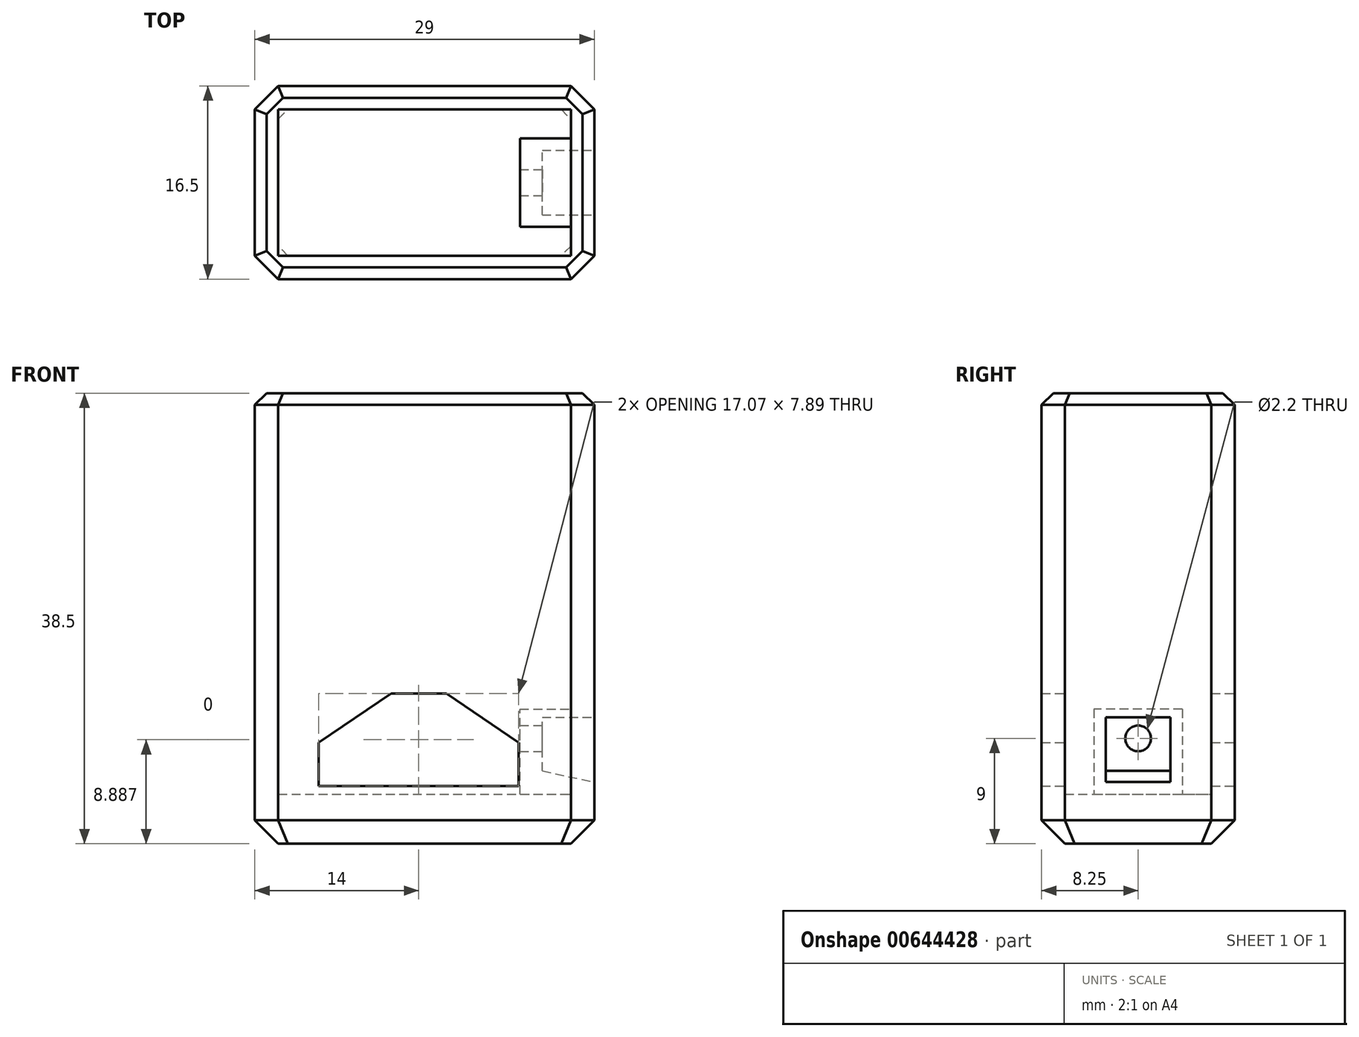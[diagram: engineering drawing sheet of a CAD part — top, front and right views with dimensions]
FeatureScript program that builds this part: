
annotation { "Feature Type Name" : "Feature", "Feature Type Description" : "" }
export const myFeature = defineFeature(function(context is Context, id is Id, definition is map)
    precondition{}
    {
        {
            var Q0;
            Q0=qCreatedBy(makeId("Top.planeOp"),FACE);
            var sketch = newSketch(context, id + "F0", { "sketchPlane" : qUnion([Q0])});
            skLineSegment(sketch, "E0.bottom", {"start": v(0, 0) * mm, "end": v(29, 0) * mm});
            skLineSegment(sketch, "E0.top", {"start": v(0, 16.5) * mm, "end": v(29, 16.5) * mm});
            skLineSegment(sketch, "E0.left", {"start": v(0, 0) * mm, "end": v(0, 16.5) * mm});
            skLineSegment(sketch, "E0.right", {"start": v(29, 0) * mm, "end": v(29, 16.5) * mm});
            skSolve(sketch);
        }
        {
            var Q0;
            Q0 = qSketchRegion(id + "F0", true);
            extrude(context, id + "F1", {"entities" : qUnion([Q0]), "depth" : 38.5 * mm, "offsetDistance" : 25 * mm});
        }
        {
            var Q0;
            Q0=makeQuery(id+"F1.opExtrude","CAP_FACE",FACE,{"disambiguationData":[OSD([sQuery(id+"F0.wireOp",EDGE,"E0.bottom"),sQuery(id+"F0.wireOp",EDGE,"E0.top"),sQuery(id+"F0.wireOp",EDGE,"E0.left"),sQuery(id+"F0.wireOp",EDGE,"E0.right")])],"isStart":false});
            shell(context, id + "F2", {"entities" : qUnion([Q0]), "thickness" : 2 * mm});
        }
        {
            var Q0;
            Q0=makeQuery(id+"F2.opShell","OFFSET_FACE",FACE,{"disambiguationData":[OSD([sQuery(id+"F0.wireOp",EDGE,"E0.bottom"),sQuery(id+"F0.wireOp",EDGE,"E0.top"),sQuery(id+"F0.wireOp",EDGE,"E0.left"),sQuery(id+"F0.wireOp",EDGE,"E0.right")])]});
            extrude(context, id + "F3", {"entities" : qUnion([Q0]), "operationType" : NewBodyOperationType.ADD, "depth" : 2.25 * mm, "offsetDistance" : 25 * mm});
        }
        {
            var Q0;
            Q0=makeQuery(id+"F1.opExtrude","SWEPT_EDGE",EDGE,{"disambiguationData":[OSD([sQuery(id+"F0.wireOp",EDGE,"E0.bottom"),sQuery(id+"F0.wireOp",EDGE,"E0.right")])]});
            var Q1;
            Q1=makeQuery(id+"F1.opExtrude","SWEPT_EDGE",EDGE,{"disambiguationData":[OSD([sQuery(id+"F0.wireOp",EDGE,"E0.top"),sQuery(id+"F0.wireOp",EDGE,"E0.right")])]});
            var Q2;
            Q2=makeQuery(id+"F1.opExtrude","SWEPT_EDGE",EDGE,{"disambiguationData":[OSD([sQuery(id+"F0.wireOp",EDGE,"E0.bottom"),sQuery(id+"F0.wireOp",EDGE,"E0.left")])]});
            var Q3;
            Q3=makeQuery(id+"F1.opExtrude","SWEPT_EDGE",EDGE,{"disambiguationData":[OSD([sQuery(id+"F0.wireOp",EDGE,"E0.top"),sQuery(id+"F0.wireOp",EDGE,"E0.left")])]});
            chamfer(context, id + "F4", {"entities" : qUnion([Q0, Q1, Q2, Q3]), "width" : 2 * mm, "tangentPropagation" : true});
        }
        {
            var Q0;
            Q0=makeQuery(id+"F1.opExtrude","CAP_EDGE",EDGE,{"disambiguationData":[OSD([sQuery(id+"F0.wireOp",EDGE,"E0.bottom")])],"isStart":true});
            var Q1;
            {var subQ0=sQuery(id+"F0.wireOp",EDGE,"E0.right");var subQ1=sQuery(id+"F0.wireOp",EDGE,"E0.bottom");Q1=makeQuery(id+"F4.opChamfer","BLEND_EDGE",EDGE,{"blendedFrom":[makeQuery(id+"F1.opExtrude","SWEPT_EDGE",EDGE,{"disambiguationData":[OSD([subQ1,subQ0])]}),makeQuery(id+"F1.opExtrude","CAP_FACE",FACE,{"disambiguationData":[OSD([subQ1,sQuery(id+"F0.wireOp",EDGE,"E0.top"),sQuery(id+"F0.wireOp",EDGE,"E0.left"),subQ0])],"isStart":true})],"blendedInto":[makeQuery(id+"F1.opExtrude","CAP_FACE",FACE,{"disambiguationData":[OSD([subQ1,sQuery(id+"F0.wireOp",EDGE,"E0.top"),sQuery(id+"F0.wireOp",EDGE,"E0.left"),subQ0])],"isStart":true})]});}
            var Q2;
            Q2=makeQuery(id+"F1.opExtrude","CAP_EDGE",EDGE,{"disambiguationData":[OSD([sQuery(id+"F0.wireOp",EDGE,"E0.right")])],"isStart":true});
            var Q3;
            {var subQ0=sQuery(id+"F0.wireOp",EDGE,"E0.right");var subQ1=sQuery(id+"F0.wireOp",EDGE,"E0.top");Q3=makeQuery(id+"F4.opChamfer","BLEND_EDGE",EDGE,{"blendedFrom":[makeQuery(id+"F1.opExtrude","SWEPT_EDGE",EDGE,{"disambiguationData":[OSD([subQ1,subQ0])]}),makeQuery(id+"F1.opExtrude","CAP_FACE",FACE,{"disambiguationData":[OSD([sQuery(id+"F0.wireOp",EDGE,"E0.bottom"),subQ1,sQuery(id+"F0.wireOp",EDGE,"E0.left"),subQ0])],"isStart":true})],"blendedInto":[makeQuery(id+"F1.opExtrude","CAP_FACE",FACE,{"disambiguationData":[OSD([sQuery(id+"F0.wireOp",EDGE,"E0.bottom"),subQ1,sQuery(id+"F0.wireOp",EDGE,"E0.left"),subQ0])],"isStart":true})]});}
            var Q4;
            Q4=makeQuery(id+"F1.opExtrude","CAP_EDGE",EDGE,{"disambiguationData":[OSD([sQuery(id+"F0.wireOp",EDGE,"E0.top")])],"isStart":true});
            var Q5;
            {var subQ0=sQuery(id+"F0.wireOp",EDGE,"E0.left");var subQ1=sQuery(id+"F0.wireOp",EDGE,"E0.top");Q5=makeQuery(id+"F4.opChamfer","BLEND_EDGE",EDGE,{"blendedFrom":[makeQuery(id+"F1.opExtrude","SWEPT_EDGE",EDGE,{"disambiguationData":[OSD([subQ1,subQ0])]}),makeQuery(id+"F1.opExtrude","CAP_FACE",FACE,{"disambiguationData":[OSD([sQuery(id+"F0.wireOp",EDGE,"E0.bottom"),subQ1,subQ0,sQuery(id+"F0.wireOp",EDGE,"E0.right")])],"isStart":true})],"blendedInto":[makeQuery(id+"F1.opExtrude","CAP_FACE",FACE,{"disambiguationData":[OSD([sQuery(id+"F0.wireOp",EDGE,"E0.bottom"),subQ1,subQ0,sQuery(id+"F0.wireOp",EDGE,"E0.right")])],"isStart":true})]});}
            var Q6;
            Q6=makeQuery(id+"F1.opExtrude","CAP_EDGE",EDGE,{"disambiguationData":[OSD([sQuery(id+"F0.wireOp",EDGE,"E0.left")])],"isStart":true});
            var Q7;
            {var subQ0=sQuery(id+"F0.wireOp",EDGE,"E0.left");var subQ1=sQuery(id+"F0.wireOp",EDGE,"E0.bottom");Q7=makeQuery(id+"F4.opChamfer","BLEND_EDGE",EDGE,{"blendedFrom":[makeQuery(id+"F1.opExtrude","SWEPT_EDGE",EDGE,{"disambiguationData":[OSD([subQ1,subQ0])]}),makeQuery(id+"F1.opExtrude","CAP_FACE",FACE,{"disambiguationData":[OSD([subQ1,sQuery(id+"F0.wireOp",EDGE,"E0.top"),subQ0,sQuery(id+"F0.wireOp",EDGE,"E0.right")])],"isStart":true})],"blendedInto":[makeQuery(id+"F1.opExtrude","CAP_FACE",FACE,{"disambiguationData":[OSD([subQ1,sQuery(id+"F0.wireOp",EDGE,"E0.top"),subQ0,sQuery(id+"F0.wireOp",EDGE,"E0.right")])],"isStart":true})]});}
            chamfer(context, id + "F5", {"entities" : qUnion([Q0, Q1, Q2, Q3, Q4, Q5, Q6, Q7]), "width" : 2 * mm, "tangentPropagation" : true});
        }
        {
            var Q0;
            Q0=makeQuery(id+"F1.opExtrude","CAP_EDGE",EDGE,{"disambiguationData":[OSD([sQuery(id+"F0.wireOp",EDGE,"E0.left")])],"isStart":false});
            var Q1;
            {var subQ0=sQuery(id+"F0.wireOp",EDGE,"E0.left");var subQ1=sQuery(id+"F0.wireOp",EDGE,"E0.bottom");Q1=makeQuery(id+"F4.opChamfer","BLEND_EDGE",EDGE,{"blendedFrom":[makeQuery(id+"F1.opExtrude","SWEPT_EDGE",EDGE,{"disambiguationData":[OSD([subQ1,subQ0])]}),makeQuery(id+"F1.opExtrude","CAP_FACE",FACE,{"disambiguationData":[OSD([subQ1,sQuery(id+"F0.wireOp",EDGE,"E0.top"),subQ0,sQuery(id+"F0.wireOp",EDGE,"E0.right")])],"isStart":false})],"blendedInto":[makeQuery(id+"F1.opExtrude","CAP_FACE",FACE,{"disambiguationData":[OSD([subQ1,sQuery(id+"F0.wireOp",EDGE,"E0.top"),subQ0,sQuery(id+"F0.wireOp",EDGE,"E0.right")])],"isStart":false})]});}
            var Q2;
            Q2=makeQuery(id+"F1.opExtrude","CAP_EDGE",EDGE,{"disambiguationData":[OSD([sQuery(id+"F0.wireOp",EDGE,"E0.bottom")])],"isStart":false});
            var Q3;
            {var subQ0=sQuery(id+"F0.wireOp",EDGE,"E0.right");var subQ1=sQuery(id+"F0.wireOp",EDGE,"E0.bottom");Q3=makeQuery(id+"F4.opChamfer","BLEND_EDGE",EDGE,{"blendedFrom":[makeQuery(id+"F1.opExtrude","SWEPT_EDGE",EDGE,{"disambiguationData":[OSD([subQ1,subQ0])]}),makeQuery(id+"F1.opExtrude","CAP_FACE",FACE,{"disambiguationData":[OSD([subQ1,sQuery(id+"F0.wireOp",EDGE,"E0.top"),sQuery(id+"F0.wireOp",EDGE,"E0.left"),subQ0])],"isStart":false})],"blendedInto":[makeQuery(id+"F1.opExtrude","CAP_FACE",FACE,{"disambiguationData":[OSD([subQ1,sQuery(id+"F0.wireOp",EDGE,"E0.top"),sQuery(id+"F0.wireOp",EDGE,"E0.left"),subQ0])],"isStart":false})]});}
            var Q4;
            Q4=makeQuery(id+"F1.opExtrude","CAP_EDGE",EDGE,{"disambiguationData":[OSD([sQuery(id+"F0.wireOp",EDGE,"E0.right")])],"isStart":false});
            var Q5;
            {var subQ0=sQuery(id+"F0.wireOp",EDGE,"E0.right");var subQ1=sQuery(id+"F0.wireOp",EDGE,"E0.top");Q5=makeQuery(id+"F4.opChamfer","BLEND_EDGE",EDGE,{"blendedFrom":[makeQuery(id+"F1.opExtrude","SWEPT_EDGE",EDGE,{"disambiguationData":[OSD([subQ1,subQ0])]}),makeQuery(id+"F1.opExtrude","CAP_FACE",FACE,{"disambiguationData":[OSD([sQuery(id+"F0.wireOp",EDGE,"E0.bottom"),subQ1,sQuery(id+"F0.wireOp",EDGE,"E0.left"),subQ0])],"isStart":false})],"blendedInto":[makeQuery(id+"F1.opExtrude","CAP_FACE",FACE,{"disambiguationData":[OSD([sQuery(id+"F0.wireOp",EDGE,"E0.bottom"),subQ1,sQuery(id+"F0.wireOp",EDGE,"E0.left"),subQ0])],"isStart":false})]});}
            var Q6;
            Q6=makeQuery(id+"F1.opExtrude","CAP_EDGE",EDGE,{"disambiguationData":[OSD([sQuery(id+"F0.wireOp",EDGE,"E0.top")])],"isStart":false});
            var Q7;
            {var subQ0=sQuery(id+"F0.wireOp",EDGE,"E0.left");var subQ1=sQuery(id+"F0.wireOp",EDGE,"E0.top");Q7=makeQuery(id+"F4.opChamfer","BLEND_EDGE",EDGE,{"blendedFrom":[makeQuery(id+"F1.opExtrude","SWEPT_EDGE",EDGE,{"disambiguationData":[OSD([subQ1,subQ0])]}),makeQuery(id+"F1.opExtrude","CAP_FACE",FACE,{"disambiguationData":[OSD([sQuery(id+"F0.wireOp",EDGE,"E0.bottom"),subQ1,subQ0,sQuery(id+"F0.wireOp",EDGE,"E0.right")])],"isStart":false})],"blendedInto":[makeQuery(id+"F1.opExtrude","CAP_FACE",FACE,{"disambiguationData":[OSD([sQuery(id+"F0.wireOp",EDGE,"E0.bottom"),subQ1,subQ0,sQuery(id+"F0.wireOp",EDGE,"E0.right")])],"isStart":false})]});}
            chamfer(context, id + "F6", {"entities" : qUnion([Q0, Q1, Q2, Q3, Q4, Q5, Q6, Q7]), "width" : 1 * mm, "tangentPropagation" : true});
        }
        {
            var Q0;
            Q0=makeQuery(id+"F1.opExtrude","SWEPT_FACE",FACE,{"disambiguationData":[OSD([sQuery(id+"F0.wireOp",EDGE,"E0.top")])]});
            var sketch = newSketch(context, id + "F7", { "sketchPlane" : qUnion([Q0])});
            skLineSegment(sketch, "E1", {"start": v(-22.54, 4.94) * mm, "end": v(-5.46, 4.94) * mm});
            skLineSegment(sketch, "E2", {"start": v(-5.46, 4.94) * mm, "end": v(-5.46, 8.66) * mm});
            skLineSegment(sketch, "E3", {"start": v(-11.64, 12.83) * mm, "end": v(-16.36, 12.83) * mm});
            skLineSegment(sketch, "E4", {"start": v(-16.36, 12.83) * mm, "end": v(-22.54, 8.66) * mm});
            skLineSegment(sketch, "E5", {"start": v(-22.54, 8.66) * mm, "end": v(-22.54, 4.94) * mm});
            skLineSegment(sketch, "E6", {"start": v(-5.46, 8.66) * mm, "end": v(-11.64, 12.83) * mm});
            skSolve(sketch);
        }
        {
            var Q0;
            Q0=makeQuery(id+"F7.imprint","IMPRINT",FACE,{"disambiguationData":[TD([[makeQuery(id+"F7.imprint","IMPRINT",EDGE,{"derivedFrom":sQuery(id+"F7.wireOp",EDGE,"E1")}),1.0]])]});
            extrude(context, id + "F8", {"entities" : qUnion([Q0]), "operationType" : NewBodyOperationType.REMOVE, "endBound" : BoundingType.THROUGH_ALL, "oppositeDirection" : true, "depth" : 25 * mm, "offsetDistance" : 25 * mm});
        }
        {
            var Q0;
            Q0=makeQuery(id+"F1.opExtrude","SWEPT_FACE",FACE,{"disambiguationData":[OSD([sQuery(id+"F0.wireOp",EDGE,"E0.right")])]});
            var sketch = newSketch(context, id + "F9", { "sketchPlane" : qUnion([Q0])});
            skLineSegment(sketch, "E7.bottom", {"start": v(4.48, 4.25) * mm, "end": v(12.02, 4.25) * mm});
            skLineSegment(sketch, "E7.top", {"start": v(4.48, 11.5) * mm, "end": v(12.02, 11.5) * mm});
            skLineSegment(sketch, "E7.left", {"start": v(4.48, 4.25) * mm, "end": v(4.48, 11.5) * mm});
            skLineSegment(sketch, "E7.right", {"start": v(12.02, 4.25) * mm, "end": v(12.02, 11.5) * mm});
            skCircle(sketch, "E8", {"center": v(8.25, 9) * mm, "radius": 1.1 * mm});
            skSolve(sketch);
        }
        {
            var Q0;
            Q0=makeQuery(id+"F9.imprint","IMPRINT",FACE,{"disambiguationData":[TD([[makeQuery(id+"F9.imprint","IMPRINT",EDGE,{"derivedFrom":sQuery(id+"F9.wireOp",EDGE,"E7.bottom")}),1.0]])]});
            extrude(context, id + "F10", {"entities" : qUnion([Q0]), "operationType" : NewBodyOperationType.ADD, "oppositeDirection" : true, "depth" : 6.35 * mm, "offsetDistance" : 25 * mm});
        }
        {
            var Q0;
            Q0=makeQuery(id+"F1.opExtrude","SWEPT_FACE",FACE,{"disambiguationData":[OSD([sQuery(id+"F0.wireOp",EDGE,"E0.right")])]});
            var sketch = newSketch(context, id + "F11", { "sketchPlane" : qUnion([Q0])});
            skLineSegment(sketch, "E9.bottom", {"start": v(5.48, 10.8) * mm, "end": v(11.02, 10.8) * mm});
            skLineSegment(sketch, "E9.top", {"start": v(5.48, 5.27) * mm, "end": v(11.02, 5.27) * mm});
            skLineSegment(sketch, "E9.left", {"start": v(5.48, 10.8) * mm, "end": v(5.48, 5.27) * mm});
            skLineSegment(sketch, "E9.right", {"start": v(11.02, 10.8) * mm, "end": v(11.02, 5.27) * mm});
            skSolve(sketch);
        }
        {
            var Q0;
            Q0=makeQuery(id+"F11.imprint","IMPRINT",FACE,{"disambiguationData":[TD([[makeQuery(id+"F11.imprint","IMPRINT",EDGE,{"derivedFrom":sQuery(id+"F11.wireOp",EDGE,"E9.bottom")}),1.0]])]});
            cPlane(context, id + "F12", {"entities" : qUnion([Q0]), "cplaneType" : CPlaneType.OFFSET, "offset" : 4.45 * mm, "oppositeDirection" : true, "width" : 150 * mm, "height" : 150 * mm});
        }
        {
            var Q0;
            Q0=qCreatedBy(id+"F12.planeOp",FACE);
            var sketch = newSketch(context, id + "F13", { "sketchPlane" : qUnion([Q0])});
            skLineSegment(sketch, "E10.bottom", {"start": v(5.48, 6.22) * mm, "end": v(11.02, 6.22) * mm});
            skLineSegment(sketch, "E10.top", {"start": v(5.48, 10.8) * mm, "end": v(11.02, 10.8) * mm});
            skLineSegment(sketch, "E10.left", {"start": v(5.48, 6.22) * mm, "end": v(5.48, 10.8) * mm});
            skLineSegment(sketch, "E10.right", {"start": v(11.02, 6.22) * mm, "end": v(11.02, 10.8) * mm});
            skSolve(sketch);
        }
        {
            var Q1;
            Q1 = qSketchRegion(id + "F13", true);
            var Q2;
            Q2 = qSketchRegion(id + "F11", true);
            loft(context, id + "F14", {"operationType" : NewBodyOperationType.REMOVE, "sheetProfilesArray" : [{ "sheetProfileEntities" : qUnion([Q1]) }, { "sheetProfileEntities" : qUnion([Q2]) }]});
        }
    });
